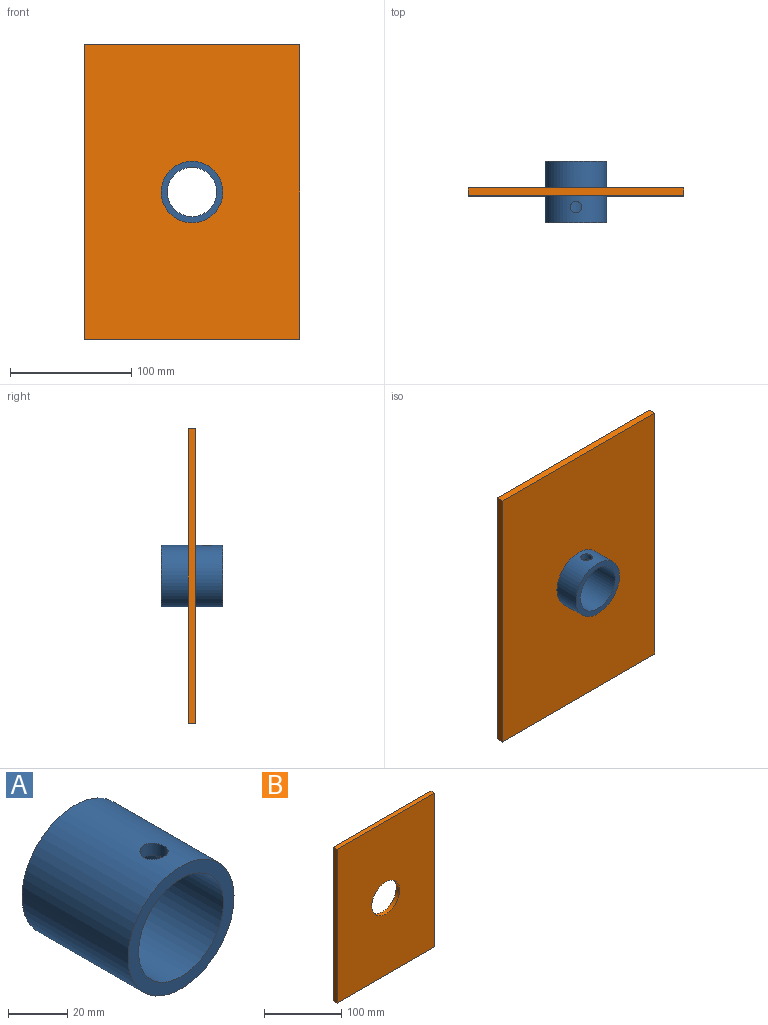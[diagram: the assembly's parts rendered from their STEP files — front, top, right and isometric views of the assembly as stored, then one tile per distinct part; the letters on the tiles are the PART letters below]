
ASSEMBLY  parts=2 mates=1
PART A: 5 faces, bbox 50.8x50.8x50.8 mm
  f0: cylinder r=20.32mm len=50.8mm, axis (0,1,0), area 6413.9mm2, adj f2,f3,f4
  f1: cylinder r=25.4mm len=50.8mm, axis (0,1,0), area 8035.4mm2, adj f2,f3,f4
  f2: plane 50.8x50.8mm, normal (0,-1,0), area 729.7mm2, adj f0,f1
  f3: plane 50.8x50.8mm, normal (0,1,0), area 729.7mm2, adj f0,f1
  f4: cylinder r=4.76mm len=9.53mm, axis (0,0,-1), area 153.7mm2, adj f0,f1
PART B: 7 faces, bbox 177.8x6.4x243.3 mm
  f0: plane 243.33x6.35mm, normal (-1,0,0), area 1545.2mm2, adj f1,f3,f4,f5
  f1: plane 177.8x6.35mm, normal (0,0,-1), area 1129mm2, adj f0,f2,f4,f5
  f2: plane 243.33x6.35mm, normal (1,0,0), area 1545.2mm2, adj f1,f3,f4,f5
  f3: plane 177.8x6.35mm, normal (0,0,1), area 1129mm2, adj f0,f2,f4,f5
  f4: plane 243.33x177.8mm, normal (0,-1,0), area 41237.6mm2, adj f0,f1,f2,f3,f6
  f5: plane 243.33x177.8mm, normal (0,1,0), area 41237.6mm2, adj f0,f1,f2,f3,f6
  f6: cylinder r=25.4mm len=50.8mm, axis (0,-1,0), area 1013.4mm2, adj f4,f5
PLACE A t=(-8.8,64.79,66.7)mm
PLACE B t=(-97.7,42.56,-54.97)mm
MATE fastened A.f1 <-> B.f6  axis (0,1,0) through (-8.8,39.39,66.7)mm
